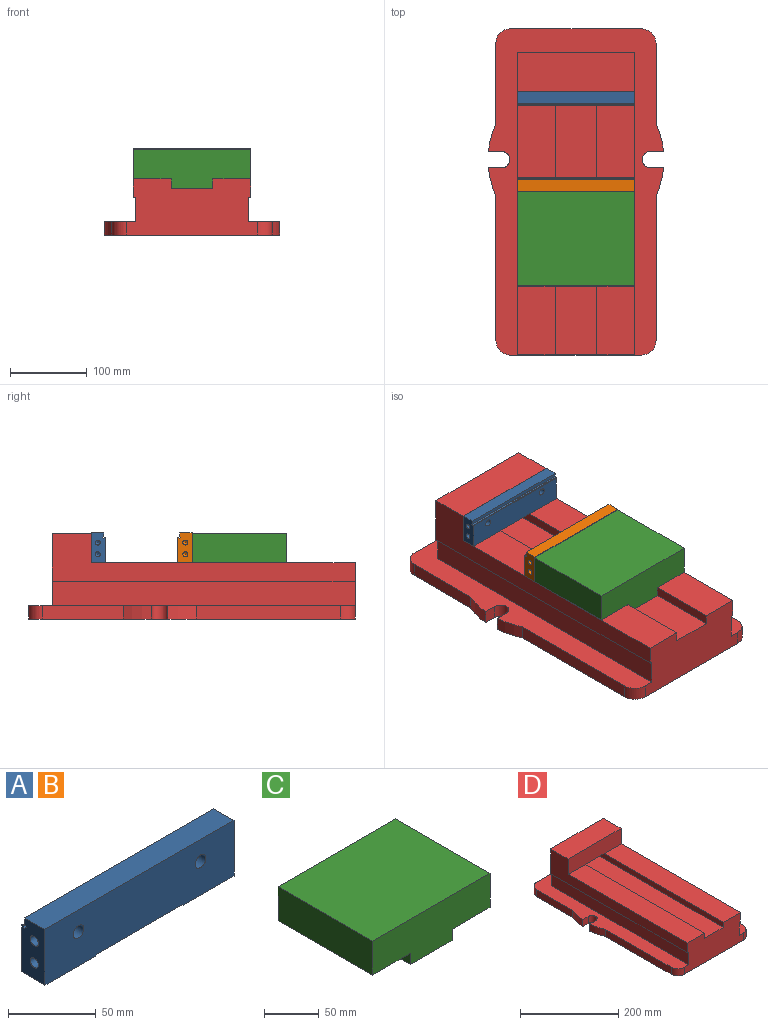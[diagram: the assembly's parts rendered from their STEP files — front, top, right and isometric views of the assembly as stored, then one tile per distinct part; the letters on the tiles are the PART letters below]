
ASSEMBLY  parts=4 mates=8
PART A: 25 faces, bbox 152.4x18.5x38.9 mm
  f0: plane 40.48x18.54mm, normal (0,0,-1), area 750.5mm2, adj f1,f2,f11,f22
  f1: plane 152.4x32.77mm, normal (0,1,0), area 4818.2mm2, adj f0,f3,f9,f10,f11,f20,f21,f22
  f2: plane 152.4x38.86mm, normal (0,-1,0), area 5747.3mm2, adj f0,f8,f9,f10,f11,f20,f21,f22
  f3: plane 152.4x0.98mm, normal (0,0,1), area 148.8mm2, adj f1,f4,f10,f11
  f4: plane 152.4x1.26mm, normal (0,-0.71,0.71), area 271mm2, adj f3,f5,f10,f11
  f5: plane 152.4x1.44mm, normal (0,0.71,0.71), area 309.7mm2, adj f4,f6,f10,f11
  f6: plane 152.4x1.26mm, normal (0,0.71,-0.71), area 271mm2, adj f5,f7,f10,f11
  f7: plane 152.4x4.66mm, normal (0,1,0), area 710.1mm2, adj f6,f8,f10,f11
  f8: plane 152.4x16.13mm, normal (0,0,1), area 2458.1mm2, adj f2,f7,f10,f11
  f9: plane 40.48x18.54mm, normal (0,0,-1), area 750.5mm2, adj f1,f2,f10,f20
  f10: plane 38.86x18.54mm, normal (1,0,0), area 636.4mm2, adj f1,f2,f3,f4,f5,f6,f7,f8
  f11: plane 38.86x18.54mm, normal (-1,0,0), area 636.4mm2, adj f0,f1,f2,f3,f4,f5,f6,f7
  f12: cone r=0mm half-angle=59deg, axis (1,0,0), area 39mm2, adj f13
  f13: cylinder r=3.26mm len=15.88mm, axis (1,0,0), area 325.6mm2, adj f10,f12
  f14: cone r=0mm half-angle=59deg, axis (1,0,0), area 39mm2, adj f15
  f15: cylinder r=3.26mm len=15.88mm, axis (1,0,0), area 325.6mm2, adj f10,f14
  f16: cone r=0mm half-angle=59deg, axis (-1,0,0), area 39mm2, adj f17
  f17: cylinder r=3.26mm len=15.88mm, axis (-1,0,0), area 325.6mm2, adj f11,f16
  f18: cone r=0mm half-angle=59deg, axis (-1,0,0), area 39mm2, adj f19
  f19: cylinder r=3.26mm len=15.88mm, axis (-1,0,0), area 325.6mm2, adj f11,f18
  f20: plane 18.54x0.79mm, normal (-0.71,0,-0.71), area 20.8mm2, adj f1,f2,f9,f21
  f21: plane 69.86x18.54mm, normal (0,0,-1), area 1295.4mm2, adj f1,f2,f20,f22
  f22: plane 18.54x0.79mm, normal (0.71,0,-0.71), area 20.8mm2, adj f0,f1,f2,f21
  f23: cylinder r=4.36mm len=18.54mm, axis (0,1,0), area 507.5mm2, adj f1,f2
  f24: cylinder r=4.36mm len=18.54mm, axis (0,1,0), area 507.5mm2, adj f1,f2
PART B: same geometry as A
PART C: 10 faces, bbox 152.4x122.2x50.8 mm
  f0: plane 152.4x122.24mm, normal (0,0,1), area 18629mm2, adj f1,f4,f6,f8
  f1: plane 122.24x38.1mm, normal (1,0,0), area 4657.2mm2, adj f0,f2,f6,f8
  f2: plane 122.24x49.21mm, normal (0,0,-1), area 6015.6mm2, adj f1,f3,f6,f8
  f3: plane 122.24x12.7mm, normal (1,0,0), area 1552.4mm2, adj f2,f5,f6,f8
  f4: plane 122.24x38.1mm, normal (-1,0,0), area 4657.2mm2, adj f0,f6,f7,f8
  f5: plane 122.24x53.98mm, normal (0,0,-1), area 6597.8mm2, adj f3,f6,f8,f9
  f6: plane 152.4x50.8mm, normal (0,-1,0), area 6491.9mm2, adj f0,f1,f2,f3,f4,f5,f7,f9
  f7: plane 122.24x49.21mm, normal (0,0,-1), area 6015.6mm2, adj f4,f6,f8,f9
  f8: plane 152.4x50.8mm, normal (0,1,0), area 6491.9mm2, adj f0,f1,f2,f3,f4,f5,f7,f9
  f9: plane 122.24x12.7mm, normal (-1,0,0), area 1552.4mm2, adj f5,f6,f7,f8
PART D: 37 faces, bbox 227.6x423.9x111.1 mm
  f0: plane 187.5x17.46mm, normal (1,0,0), area 3274.3mm2, adj f1,f18,f19,f21
  f1: cylinder r=114.3mm len=36.77mm, axis (0,0,-1), area 667.7mm2, adj f0,f2,f18,f21
  f2: plane 17.46x16.96mm, normal (0,1,0), area 296.2mm2, adj f1,f3,f18,f21
  f3: cylinder r=10.67mm len=21.35mm, axis (0,0,-1), area 585.5mm2, adj f2,f4,f18,f21
  f4: plane 17.46x16.96mm, normal (0,-1,0), area 296.2mm2, adj f3,f5,f18,f21
  f5: cylinder r=114.3mm len=36.77mm, axis (0,0,-1), area 667.7mm2, adj f4,f6,f18,f21
  f6: plane 103.37x17.46mm, normal (1,0,0), area 1805mm2, adj f5,f7,f18,f21
  f7: cylinder r=19.05mm len=19.05mm, axis (0,0,-1), area 522.5mm2, adj f6,f8,f18,f21
  f8: plane 171.12x17.46mm, normal (0,1,0), area 2988.2mm2, adj f7,f9,f18,f21
  f9: cylinder r=17.81mm len=17.81mm, axis (0,0,-1), area 488.4mm2, adj f8,f10,f18,f21
  f10: plane 104.61x17.46mm, normal (-1,0,0), area 1826.8mm2, adj f9,f11,f18,f21
  f11: cylinder r=114.3mm len=36.77mm, axis (0,0,-1), area 667.7mm2, adj f10,f12,f18,f21
  f12: plane 17.46x16.96mm, normal (0,-1,0), area 296.2mm2, adj f11,f13,f18,f21
  f13: cylinder r=10.67mm len=21.35mm, axis (0,0,-1), area 585.5mm2, adj f12,f14,f18,f21
  f14: plane 17.46x16.96mm, normal (0,1,0), area 296.2mm2, adj f13,f15,f18,f21
  f15: cylinder r=114.3mm len=36.77mm, axis (0,0,-1), area 667.7mm2, adj f14,f16,f18,f21
  f16: plane 187.5x17.46mm, normal (-1,0,0), area 3274.3mm2, adj f15,f17,f18,f21
  f17: cylinder r=19.05mm len=19.05mm, axis (0,0,-1), area 522.5mm2, adj f16,f18,f21,f27
  f18: plane 423.86x227.6mm, normal (0,0,-1), area 88071.8mm2, adj f0,f1,f2,f3,f4,f5,f6,f7
  f19: cylinder r=19.05mm len=19.05mm, axis (0,0,-1), area 522.5mm2, adj f0,f18,f21,f27
  f20: plane 393.7x31.75mm, normal (1,0,0), area 12500mm2, adj f21,f27,f28,f29
  f21: plane 423.86x227.6mm, normal (0,0,1), area 30572mm2, adj f0,f1,f2,f3,f4,f5,f6,f7
  f22: plane 393.7x31.75mm, normal (-1,0,0), area 12500mm2, adj f21,f24,f27,f29
  f23: plane 393.7x53.98mm, normal (0,0,1), area 21250mm2, adj f25,f26,f27,f29
  f24: plane 393.7x3.18mm, normal (0,0,-1), area 1250mm2, adj f22,f27,f29,f31
  f25: plane 393.7x12.7mm, normal (1,0,0), area 5000mm2, adj f23,f27,f29,f32,f33
  f26: plane 393.7x12.7mm, normal (-1,0,0), area 5000mm2, adj f23,f27,f29,f33,f34
  f27: plane 169.88x73.03mm, normal (0,-1,0), area 10547.1mm2, adj f17,f18,f19,f20,f21,f22,f23,f24
  f28: plane 393.7x3.18mm, normal (0,0,-1), area 1250mm2, adj f20,f27,f29,f35
  f29: plane 152.4x93.66mm, normal (0,1,0), area 13387.1mm2, adj f20,f21,f22,f23,f24,f25,f26,f28
  f30: plane 152.4x50.8mm, normal (0,0,1), area 7741.9mm2, adj f29,f31,f35,f36
  f31: plane 393.7x61.91mm, normal (-1,0,0), area 11310.5mm2, adj f24,f27,f29,f30,f32,f36
  f32: plane 342.9x49.21mm, normal (0,0,1), area 16875mm2, adj f25,f27,f31,f36
  f33: plane 53.98x50.8mm, normal (0,0,-1), area 2741.9mm2, adj f25,f26,f29,f36
  f34: plane 342.9x49.21mm, normal (0,0,1), area 16875mm2, adj f26,f27,f35,f36
  f35: plane 393.7x61.91mm, normal (1,0,0), area 11310.5mm2, adj f27,f28,f29,f30,f34,f36
  f36: plane 152.4x38.1mm, normal (0,-1,0), area 5806.4mm2, adj f30,f31,f32,f33,f34,f35
PLACE A rot(axis=(0,0,1),180deg) t=(0,0,0)mm
PLACE B t=(0,-131.05,0)mm
PLACE C t=(0,-131.05,0)mm
PLACE D t=(0,-146.05,-23.81)mm
MATE planar A.f11 <-> D.f35  axis (1,0,0) through (76.2,-9.12,19.07)mm
MATE planar A.f2 <-> D.f36  axis (0,1,0) through (0,0,19.53)mm
MATE planar D.f34 <-> B.f9  axis (0,0,1) through (51.59,-171.45,0)mm
MATE planar D.f32 <-> C.f7  axis (0,0,1) through (-51.59,-171.45,0)mm
MATE planar C.f1 <-> B.f12  axis (1,0,0) through (76.2,-192.16,19.05)mm
MATE planar D.f35 <-> C.f1  axis (1,0,0) through (76.2,-116.71,-6.61)mm
MATE planar B.f2 <-> C.f8  axis (0,-1,0) through (0,-131.05,19.53)mm
MATE planar A.f0 <-> D.f34  axis (0,0,-1) through (55.96,-9.27,0)mm
